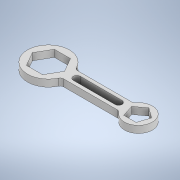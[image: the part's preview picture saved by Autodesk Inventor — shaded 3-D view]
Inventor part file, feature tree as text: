
AUTODESK INVENTOR PART (.ipt)
format: ipt  version: 2020 (Build 240168000, 168)  size: 142,336 bytes
history: native  units: mm
features: extrude x1, sketch x1
ambient origin geometry x8: Origin, YZ Plane, XZ Plane, XY Plane, X Axis, Y Axis, Z Axis, Center Point
bodies: Solid1 (feature_tree)
feature tree (2):
  extrude  "Extrusion1"  Depth=20.0mm
  sketch  "Sketch2"  dims[d14=60.0mm d15=20.0mm d16=40.0mm d17=15.0mm d24=129.0mm d25=60.0mm d26=10.0mm d27=5.0mm d28=5.0mm d29=10.0mm d30=0.0mm]
